# Revit family: Diffuser_C-Series_Angled-Square
name_source: partatom
category: Air Terminals
revit_build: Autodesk Revit 2016 (Build: 20150714_1515(x64)
units: mm (PartAtom-declared; Revit-internal decimal feet)

## family parameters
Always vertical = No
Cut with Voids When Loaded = No
OmniClass Number = 23.75.70.21.27.11
OmniClass Title = Diffusers, Registers, and Grilles
Part Type = Normal
Room Calculation Point = No
Round Connector Dimension = Use Diameter
Shared = No
Work Plane-Based = No

## types (6) — shared parameters
Assembly Code = D3040100
Diffuser Height = 1' - 3"
Diffuser Material = Polyester Fabric
Keynote = 23 37 00
Manufacturer = DuctSox
Thickness = 0' - 0 1/8"
URL = https://www.ductsox.com

## per-type parameters (varying)
| type | Bottom Diameter | Description | Inlet Size | Max Flow | Model | Top Diameter | TopRad |
| 30 Ton | 5' - 0" | Fabric Duct Diffuser - 30 Ton | 3' - 6" | 12000 CFM | C-Series Diffuser - 30 Ton | 6' - 6" | 3' - 3" |
| 25 Ton | 4' - 6" | Fabric Duct Diffuser - 25 Ton | 3' - 2" | 10000 CFM | C-Series Diffuser - 25 Ton | 6' - 0" | 3' - 0" |
| 20 Ton | 4' - 0" | Fabric Duct Diffuser - 20 Ton | 2' - 10" | 8000 CFM | C-Series Diffuser - 20 Ton | 5' - 6" | 2' - 9" |
| 15 Ton | 3' - 6" | Fabric Duct Diffuser - 15 Ton | 2' - 6" | 6000 CFM | C-Series Diffuser - 15 Ton | 5' - 0" | 2' - 6" |
| 10 Ton | 2' - 10" | Fabric Duct Diffuser - 10 Ton | 2' - 0" | 4000 CFM | C-Series Diffuser - 10 Ton | 4' - 4" | 2' - 2" |
| 5 Ton | 2' - 2" | Fabric Duct Diffuser - 5 Ton | 1' - 6" | 2000 CFM | C-Series Diffuser - 5 Ton | 3' - 8" | 1' - 10" |

## geometry (parser evidence)
native form markers: Sweep x3
no freeform markers — native parametric forms only
